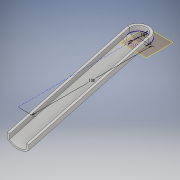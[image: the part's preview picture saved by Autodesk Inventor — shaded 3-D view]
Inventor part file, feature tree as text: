
AUTODESK INVENTOR PART (.ipt)
format: ipt  version: 2019 (Build 230136000, 136)  size: 142,336 bytes
history: native  units: mm
features: sketch x5, other x2, extrude x2, mirror x1, sweep x1
ambient origin geometry x8: Origin, YZ Plane, XZ Plane, XY Plane, X Axis, Y Axis, Z Axis, Center Point
bodies: Solide1 (feature_tree)
feature tree (11):
  sketch  "Esquisse1"
  other  "Plan de construction1"
  extrude  "Extrusion1"  Depth=100.0mm
  mirror  "Symétrie1"
  other  "Plan de construction2"
  extrude  "Extrusion2"  Depth=14.0mm
  sweep  "Balayage2"
  sketch  "Esquisse3"
  sketch  "Esquisse4"
  sketch  "Esquisse5"
  sketch  "Esquisse 3D1"
